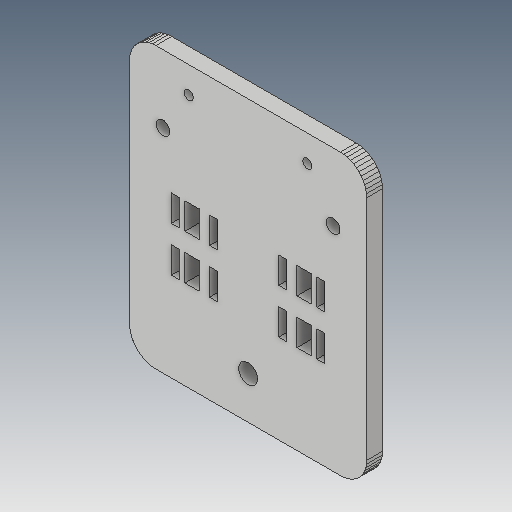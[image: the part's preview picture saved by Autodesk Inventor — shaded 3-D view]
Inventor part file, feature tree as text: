
AUTODESK INVENTOR PART (.ipt)
format: ipt  version: 2017 (Build 210142000, 142)  size: 311,296 bytes
history: native  units: mm
features: sketch x4, other x3
ambient origin geometry x8: Origin, YZ Plane, XZ Plane, XY Plane, X Axis, Y Axis, Z Axis, Center Point
bodies: Solid1 (feature_tree)
feature tree (7):
  other  "X-Axis-End-Plate.ipt"
  other  "Solid1::X-Axis-End-Plate.ipt"
  other  "TaggingFeature1"
  sketch  "Sketch1"  dims[d0=10.0mm]
  sketch  "Sketch2"
  sketch  "Sketch3"
  sketch  "Sketch4"
